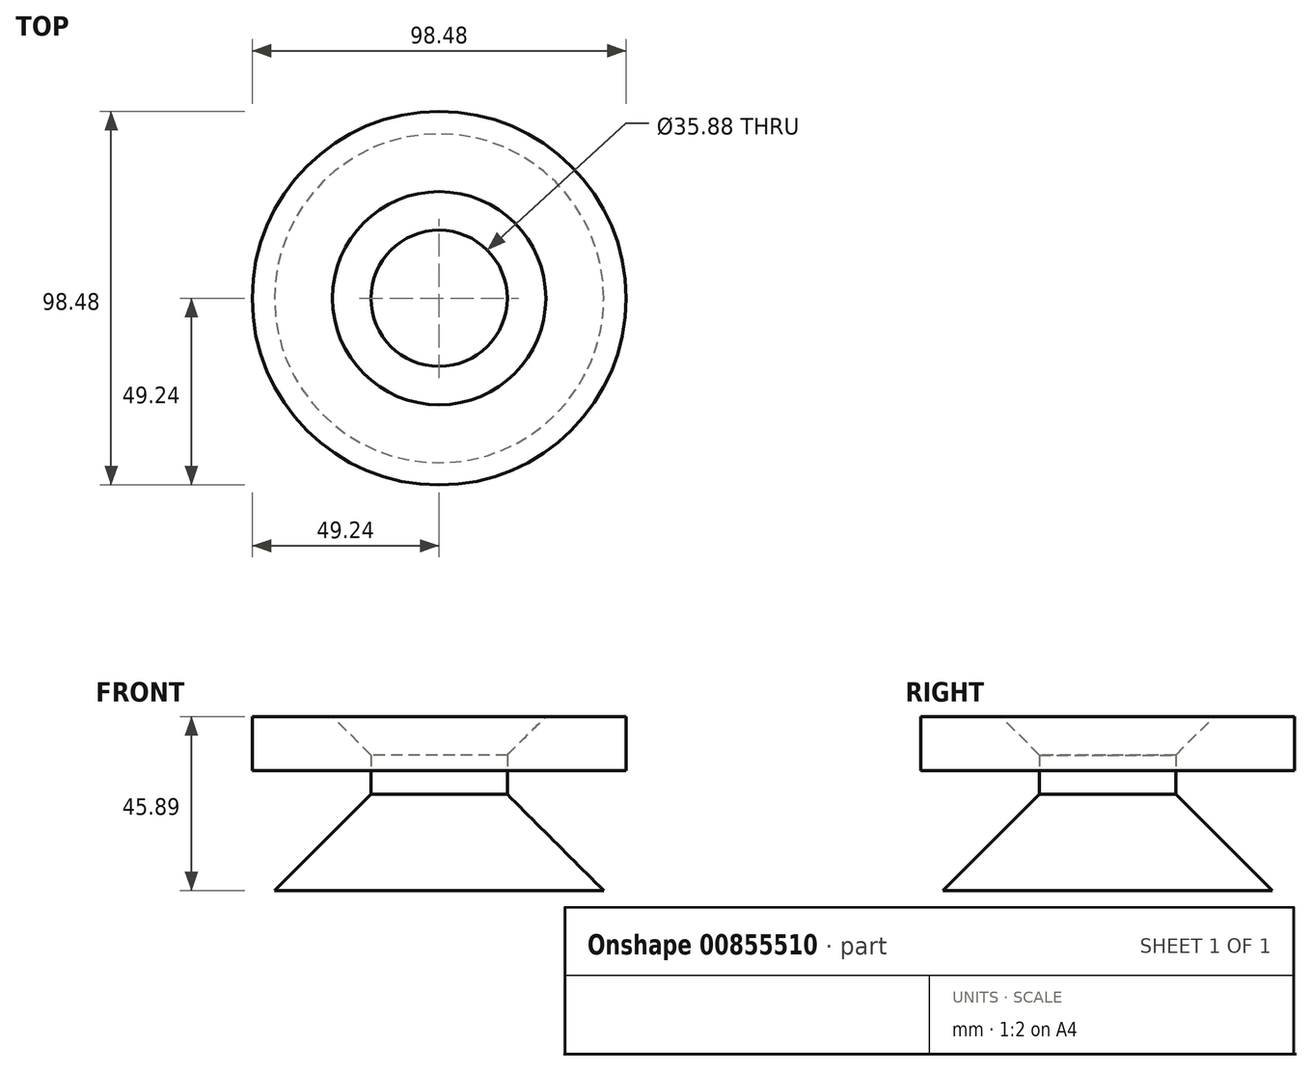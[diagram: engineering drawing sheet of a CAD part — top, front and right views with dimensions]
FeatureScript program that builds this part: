
annotation { "Feature Type Name" : "Feature", "Feature Type Description" : "" }
export const myFeature = defineFeature(function(context is Context, id is Id, definition is map)
    precondition{}
    {
        {
            var Q0;
            Q0=qCreatedBy(makeId("Top.planeOp"),FACE);
            var sketch = newSketch(context, id + "F0", { "sketchPlane" : qUnion([Q0])});
            skCircle(sketch, "E0", {"center": v(0, 0) * mm, "radius": 43.34 * mm});
            skSolve(sketch);
        }
        {
            var Q0;
            Q0=makeQuery(id+"F0.imprint","IMPRINT",FACE,{"disambiguationData":[TD([[makeQuery(id+"F0.imprint","IMPRINT",EDGE,{"derivedFrom":sQuery(id+"F0.wireOp",EDGE,"E0")}),1.0]])]});
            extrude(context, id + "F1", {"entities" : qUnion([Q0]), "depth" : 25.4 * mm, "offsetDistance" : 25.4 * mm});
        }
        {
            var Q0;
            Q0=makeQuery(id+"F1.opExtrude","CAP_FACE",FACE,{"disambiguationData":[OSD([sQuery(id+"F0.wireOp",EDGE,"E0")])],"isStart":false});
            chamfer(context, id + "F2", {"entities" : qUnion([Q0]), "width" : 25.4 * mm, "tangentPropagation" : true});
        }
        {
            var Q0;
            Q0=makeQuery(id+"F1.opExtrude","CAP_FACE",FACE,{"disambiguationData":[OSD([sQuery(id+"F0.wireOp",EDGE,"E0")])],"isStart":false});
            extrude(context, id + "F3", {"entities" : qUnion([Q0]), "operationType" : NewBodyOperationType.ADD, "depth" : 6.27 * mm, "offsetDistance" : 25.4 * mm});
        }
        {
            var Q0;
            Q0=makeQuery(id+"F3.opExtrude","CAP_FACE",FACE,{"disambiguationData":[OSD([sQuery(id+"F0.wireOp",EDGE,"E0")])],"isStart":false});
            var sketch = newSketch(context, id + "F4", { "sketchPlane" : qUnion([Q0])});
            skCircle(sketch, "E1", {"center": v(0, 0) * mm, "radius": 49.24 * mm});
            skSolve(sketch);
        }
        {
            var Q0;
            Q0=makeQuery(id+"F4.imprint","IMPRINT",FACE,{"disambiguationData":[TD([[makeQuery(id+"F4.imprint","IMPRINT",EDGE,{"derivedFrom":sQuery(id+"F4.wireOp",EDGE,"E1")}),1.0]])]});
            extrude(context, id + "F5", {"entities" : qUnion([Q0]), "depth" : 14.22 * mm, "offsetDistance" : 25.4 * mm});
        }
        {
            var Q0;
            Q0=makeQuery(id+"F5.opExtrude","CAP_EDGE",EDGE,{"disambiguationData":[OSD([sQuery(id+"F0.wireOp",EDGE,"E0")])],"isStart":false});
            chamfer(context, id + "F6", {"entities" : qUnion([Q0]), "width" : 10.16 * mm, "tangentPropagation" : true});
        }
    });
